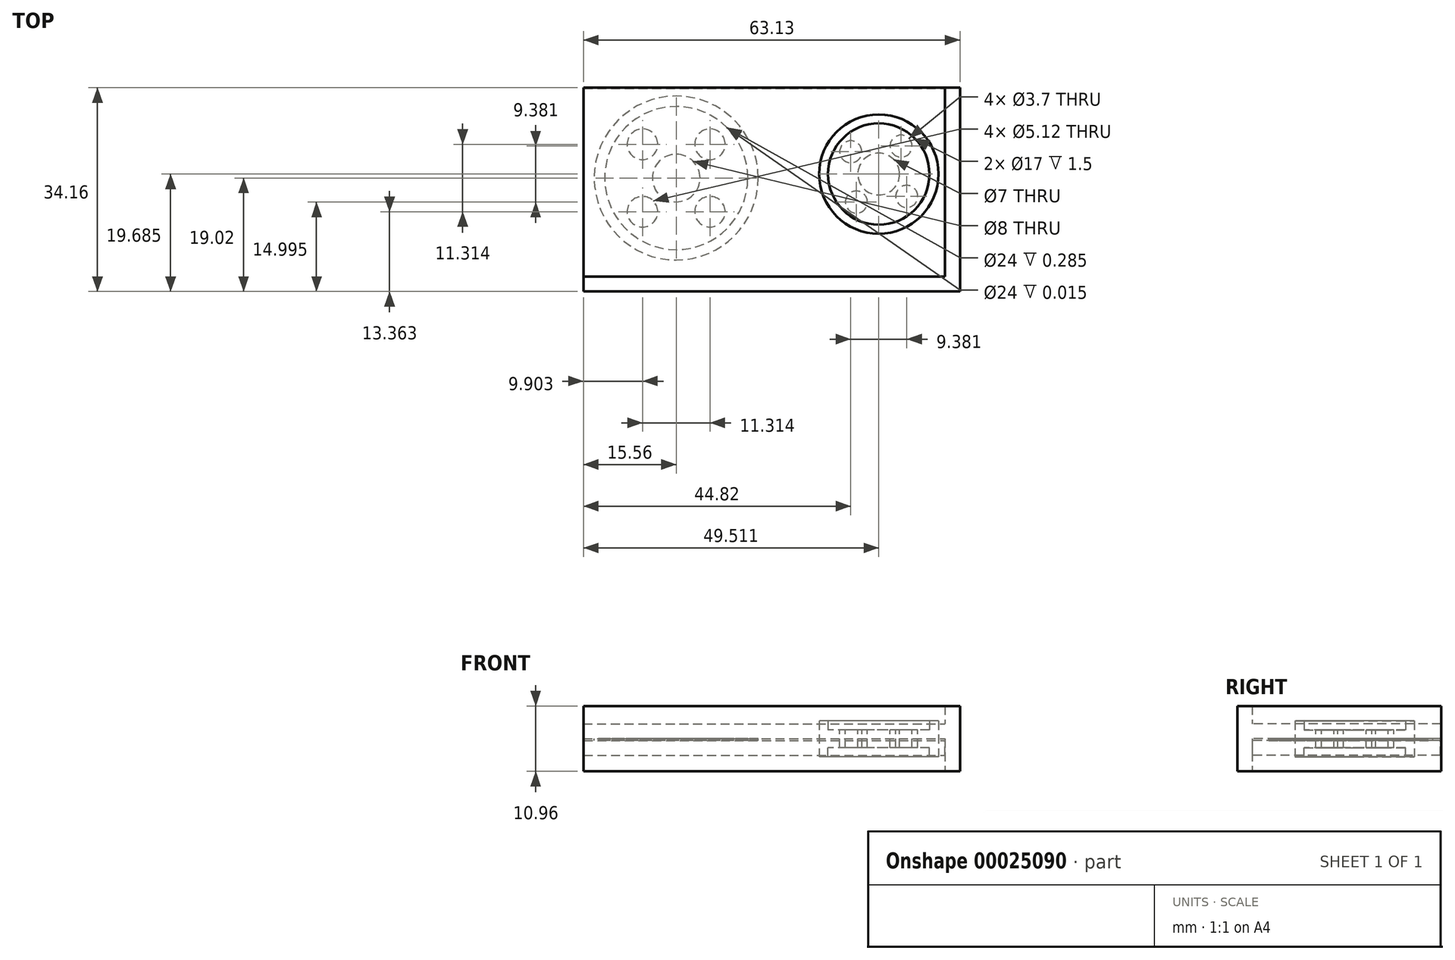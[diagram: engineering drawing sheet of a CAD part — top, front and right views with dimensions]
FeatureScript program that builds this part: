
annotation { "Feature Type Name" : "Feature", "Feature Type Description" : "" }
export const myFeature = defineFeature(function(context is Context, id is Id, definition is map)
    precondition{}
    {
        {
            var Q0;
            Q0=qCreatedBy(makeId("Top.planeOp"),FACE);
            var sketch = newSketch(context, id + "F0", { "sketchPlane" : qUnion([Q0])});
            skCircle(sketch, "E0", {"center": v(0, 0) * mm, "radius": 13.75 * mm});
            skCircle(sketch, "E1", {"center": v(0, 0) * mm, "radius": 12 * mm});
            skCircle(sketch, "E2", {"center": v(-5.66, 5.66) * mm, "radius": 2.56 * mm});
            skCircle(sketch, "E3", {"center": v(0, 0) * mm, "radius": 4 * mm});
            skCircle(sketch, "E4.1.0", {"center": v(-5.66, -5.66) * mm, "radius": 2.56 * mm});
            skCircle(sketch, "E4.2.0", {"center": v(5.66, -5.66) * mm, "radius": 2.56 * mm});
            skCircle(sketch, "E5.1.3.0", {"center": v(5.66, 5.66) * mm, "radius": 2.56 * mm});
            skLineSegment(sketch, "E6", {"start": v(0, 0) * mm, "end": v(6.52, 0) * mm, "construction": true});
            skLineSegment(sketch, "E7", {"start": v(5.66, 5.66) * mm, "end": v(5.66, -5.66) * mm, "construction": true});
            skLineSegment(sketch, "E8", {"start": v(0, 0) * mm, "end": v(-8.46, 0) * mm, "construction": true});
            skLineSegment(sketch, "E9", {"start": v(-5.66, 5.66) * mm, "end": v(-5.66, -5.66) * mm, "construction": true});
            skLineSegment(sketch, "E10", {"start": v(-5.66, 5.66) * mm, "end": v(5.66, 5.66) * mm, "construction": true});
            skLineSegment(sketch, "E11", {"start": v(-5.66, -5.66) * mm, "end": v(5.66, -5.66) * mm, "construction": true});
            skCircle(sketch, "E12", {"center": v(33.95, 0.67) * mm, "radius": 3.5 * mm});
            skCircle(sketch, "E13", {"center": v(33.95, 0.67) * mm, "radius": 8.5 * mm});
            skCircle(sketch, "E14", {"center": v(33.95, 0.67) * mm, "radius": 10 * mm});
            skCircle(sketch, "E15", {"center": v(37.7, 5.36) * mm, "radius": 1.85 * mm});
            skCircle(sketch, "E16.1.0", {"center": v(29.26, 4.4) * mm, "radius": 1.85 * mm});
            skCircle(sketch, "E16.2.0", {"center": v(30.2, -4.03) * mm, "radius": 1.85 * mm});
            skCircle(sketch, "E16.3.0", {"center": v(38.64, -3.08) * mm, "radius": 1.85 * mm});
            skSolve(sketch);
        }
        {
            var Q0;
            Q0=makeQuery(id+"F0.imprint","IMPRINT",FACE,{"disambiguationData":[TD([[makeQuery(id+"F0.imprint","IMPRINT",EDGE,{"derivedFrom":sQuery(id+"F0.wireOp",EDGE,"E1")}),1.0]])]});
            extrude(context, id + "F1", {"entities" : qUnion([Q0]), "depth" : ((3 / 5) / 2) / 20 * mm});
        }
        {
            var Q0;
            Q0=makeQuery(id+"F0.imprint","IMPRINT",FACE,{"disambiguationData":[TD([[makeQuery(id+"F0.imprint","IMPRINT",EDGE,{"derivedFrom":sQuery(id+"F0.wireOp",EDGE,"E1")}),1.0]])]});
            extrude(context, id + "F2", {"entities" : qUnion([Q0]), "operationType" : NewBodyOperationType.ADD, "oppositeDirection" : true, "depth" : ((3 / 5) / 2) / 20 * mm});
        }
        {
            var Q0;
            Q0=makeQuery(id+"F0.imprint","IMPRINT",FACE,{"disambiguationData":[TD([[makeQuery(id+"F0.imprint","IMPRINT",EDGE,{"derivedFrom":sQuery(id+"F0.wireOp",EDGE,"E0")}),1.0]])]});
            extrude(context, id + "F3", {"entities" : qUnion([Q0]), "operationType" : NewBodyOperationType.ADD, "oppositeDirection" : true, "depth" : ((3 / 5) / 2) * mm});
        }
        {
            var Q0;
            Q0=makeQuery(id+"F0.imprint","IMPRINT",FACE,{"disambiguationData":[TD([[makeQuery(id+"F0.imprint","IMPRINT",EDGE,{"derivedFrom":sQuery(id+"F0.wireOp",EDGE,"E0")}),1.0]])]});
            extrude(context, id + "F4", {"entities" : qUnion([Q0]), "operationType" : NewBodyOperationType.ADD, "depth" : (3 / 5) / 20 * mm});
        }
        {
            var Q0;
            Q0=makeQuery(id+"F0.imprint","IMPRINT",FACE,{"disambiguationData":[TD([[makeQuery(id+"F0.imprint","IMPRINT",EDGE,{"derivedFrom":sQuery(id+"F0.wireOp",EDGE,"E12")}),-1.0]])]});
            extrude(context, id + "F5", {"entities" : qUnion([Q0]), "oppositeDirection" : true, "depth" : 1.5 * mm});
        }
        {
            var Q0;
            Q0=makeQuery(id+"F0.imprint","IMPRINT",FACE,{"disambiguationData":[TD([[makeQuery(id+"F0.imprint","IMPRINT",EDGE,{"derivedFrom":sQuery(id+"F0.wireOp",EDGE,"E12")}),-1.0]])]});
            extrude(context, id + "F6", {"entities" : qUnion([Q0]), "operationType" : NewBodyOperationType.ADD, "depth" : 1.5 * mm});
        }
        {
            var Q0;
            Q0=makeQuery(id+"F0.imprint","IMPRINT",FACE,{"disambiguationData":[TD([[makeQuery(id+"F0.imprint","IMPRINT",EDGE,{"derivedFrom":sQuery(id+"F0.wireOp",EDGE,"E13")}),-1.0]])]});
            extrude(context, id + "F7", {"entities" : qUnion([Q0]), "operationType" : NewBodyOperationType.ADD, "depth" : 3 * mm});
        }
        {
            var Q0;
            Q0=makeQuery(id+"F0.imprint","IMPRINT",FACE,{"disambiguationData":[TD([[makeQuery(id+"F0.imprint","IMPRINT",EDGE,{"derivedFrom":sQuery(id+"F0.wireOp",EDGE,"E13")}),-1.0]])]});
            extrude(context, id + "F8", {"entities" : qUnion([Q0]), "operationType" : NewBodyOperationType.ADD, "oppositeDirection" : true, "depth" : 3 * mm});
        }
        {
            var Q0;
            Q0=makeQuery(id+"F3.opExtrude","CAP_FACE",FACE,{"disambiguationData":[OSD([sQuery(id+"F0.wireOp",EDGE,"E0"),sQuery(id+"F0.wireOp",EDGE,"E1")])],"isStart":false});
            var sketch = newSketch(context, id + "F9", { "sketchPlane" : qUnion([Q0])});
            skLineSegment(sketch, "E17.bottom", {"start": v(-15.51, 16.46) * mm, "end": v(45.1, 16.46) * mm});
            skLineSegment(sketch, "E17.top", {"start": v(-15.51, -15) * mm, "end": v(45.1, -15) * mm});
            skLineSegment(sketch, "E17.left", {"start": v(-15.51, 16.46) * mm, "end": v(-15.51, -15) * mm});
            skLineSegment(sketch, "E17.right", {"start": v(45.1, 16.46) * mm, "end": v(45.1, -15) * mm});
            skSolve(sketch);
        }
        {
            var Q0;
            Q0 = qSketchRegion(id + "F9", true);
            extrude(context, id + "F10", {"entities" : qUnion([Q0]), "depth" : 2.5 * mm});
        }
        {
            var Q0;
            Q0=makeQuery(id+"F4.opExtrude","CAP_FACE",FACE,{"disambiguationData":[OSD([sQuery(id+"F0.wireOp",EDGE,"E0"),sQuery(id+"F0.wireOp",EDGE,"E1")])],"isStart":false});
            var sketch = newSketch(context, id + "F11", { "sketchPlane" : qUnion([Q0])});
            skLineSegment(sketch, "E18.bottom", {"start": v(-15.56, 15.14) * mm, "end": v(45.07, 15.14) * mm});
            skLineSegment(sketch, "E18.top", {"start": v(-15.56, -16.52) * mm, "end": v(45.07, -16.52) * mm});
            skLineSegment(sketch, "E18.left", {"start": v(-15.56, 15.14) * mm, "end": v(-15.56, -16.52) * mm});
            skLineSegment(sketch, "E18.right", {"start": v(45.07, 15.14) * mm, "end": v(45.07, -16.52) * mm});
            skSolve(sketch);
        }
        {
            var Q0;
            Q0 = qSketchRegion(id + "F11", true);
            extrude(context, id + "F12", {"entities" : qUnion([Q0]), "depth" : 2.5 * mm});
        }
        {
            var Q0;
            Q0=makeQuery(id+"F12.opExtrude","SWEPT_FACE",FACE,{"disambiguationData":[OSD([sQuery(id+"F11.wireOp",EDGE,"E18.top")])]});
            var sketch = newSketch(context, id + "F13", { "sketchPlane" : qUnion([Q0])});
            skLineSegment(sketch, "E19.bottom", {"start": v(-15.56, 5.5) * mm, "end": v(45.07, 5.5) * mm});
            skLineSegment(sketch, "E19.top", {"start": v(-15.56, -5.46) * mm, "end": v(45.07, -5.46) * mm});
            skLineSegment(sketch, "E19.left", {"start": v(-15.56, 5.5) * mm, "end": v(-15.56, -5.46) * mm});
            skLineSegment(sketch, "E19.right", {"start": v(45.07, 5.5) * mm, "end": v(45.07, -5.46) * mm});
            skSolve(sketch);
        }
        {
            var Q0;
            Q0 = qSketchRegion(id + "F13", true);
            extrude(context, id + "F14", {"entities" : qUnion([Q0]), "operationType" : NewBodyOperationType.ADD, "depth" : 2.5 * mm});
        }
        {
            var Q0;
            Q0=makeQuery(id+"F14.boolean.opBoolean","MERGE",FACE,{"derivedFrom":[makeQuery(id+"F12.opExtrude","SWEPT_FACE",FACE,{"disambiguationData":[OSD([sQuery(id+"F11.wireOp",EDGE,"E18.right")])]}),makeQuery(id+"F14.opExtrude","SWEPT_FACE",FACE,{"disambiguationData":[OSD([sQuery(id+"F13.wireOp",EDGE,"E19.right")])]})]});
            var sketch = newSketch(context, id + "F15", { "sketchPlane" : qUnion([Q0])});
            skLineSegment(sketch, "E20.bottom", {"start": v(-19.02, 5.5) * mm, "end": v(15.14, 5.5) * mm});
            skLineSegment(sketch, "E20.top", {"start": v(-19.02, -5.46) * mm, "end": v(15.14, -5.46) * mm});
            skLineSegment(sketch, "E20.left", {"start": v(-19.02, 5.5) * mm, "end": v(-19.02, -5.46) * mm});
            skLineSegment(sketch, "E20.right", {"start": v(15.14, 5.5) * mm, "end": v(15.14, -5.46) * mm});
            skSolve(sketch);
        }
        {
            var Q0;
            Q0 = qSketchRegion(id + "F15", true);
            extrude(context, id + "F16", {"entities" : qUnion([Q0]), "operationType" : NewBodyOperationType.ADD, "depth" : 2.5 * mm});
        }
    });
